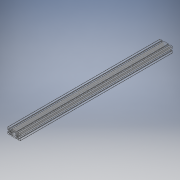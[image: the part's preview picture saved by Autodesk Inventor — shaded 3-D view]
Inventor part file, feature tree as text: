
AUTODESK INVENTOR PART (.ipt)
format: ipt  version: 2019 (Build 230136000, 136)  size: 325,632 bytes
history: native  units: in
note: dims shown in document units (in); Inventor stores cm internally (conversion verified against a paired STEP export)
features: extrude x1, sketch x1
ambient origin geometry x8: Origin, YZ Plane, XZ Plane, XY Plane, X Axis, Y Axis, Z Axis, Center Point
bodies: Solid1 (feature_tree)
feature tree (2):
  extrude  "Extrusion1"  [1 undecoded]
  sketch  "Sketch1"  dims[d0=36.0in d1=0.0in]
note: 1 required parameter value undecoded (feature->parameter linkage not recoverable at this tier; creation-order binding heuristic only, values carry confidence <= 0.55)
